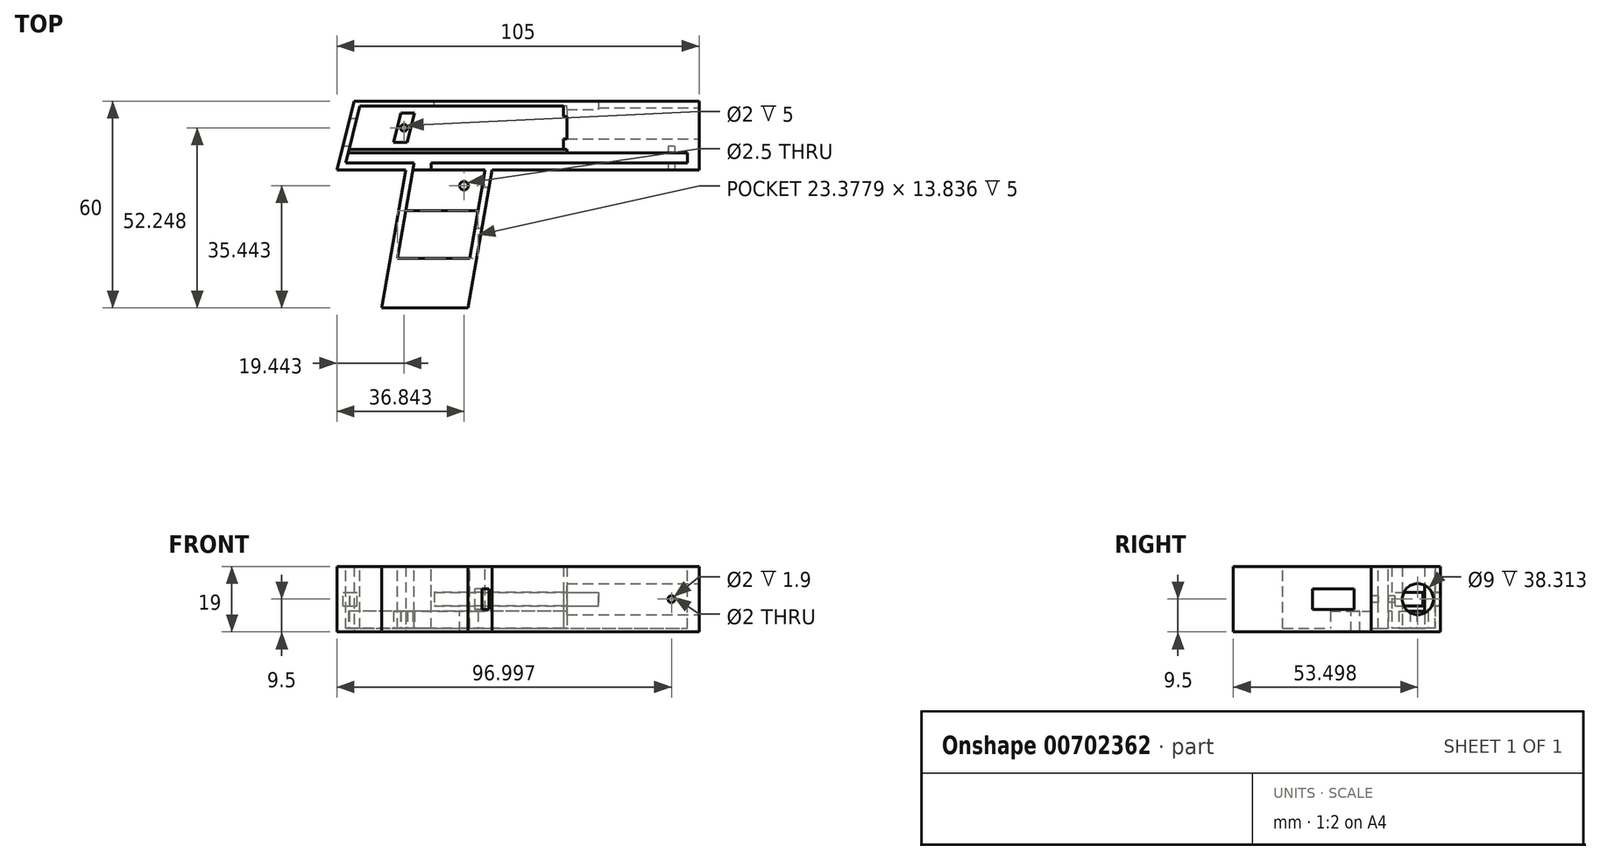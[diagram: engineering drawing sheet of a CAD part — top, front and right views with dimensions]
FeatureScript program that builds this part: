
annotation { "Feature Type Name" : "Feature", "Feature Type Description" : "" }
export const myFeature = defineFeature(function(context is Context, id is Id, definition is map)
    precondition{}
    {
        {
            var Q0;
            Q0=qCreatedBy(makeId("Top.planeOp"),FACE);
            var sketch = newSketch(context, id + "F0", { "sketchPlane" : qUnion([Q0])});
            skLineSegment(sketch, "E0", {"start": v(-39.8, 26.27) * mm, "end": v(60.2, 26.27) * mm});
            skLineSegment(sketch, "E1", {"start": v(60.2, 26.27) * mm, "end": v(60.2, 6.27) * mm});
            skLineSegment(sketch, "E2", {"start": v(60.2, 6.27) * mm, "end": v(0.2, 6.27) * mm});
            skLineSegment(sketch, "E3", {"start": v(0.2, 6.27) * mm, "end": v(-6.86, -33.73) * mm});
            skLineSegment(sketch, "E4", {"start": v(-6.86, -33.73) * mm, "end": v(-31.86, -33.73) * mm});
            skLineSegment(sketch, "E5", {"start": v(-31.86, -33.73) * mm, "end": v(-24.8, 6.27) * mm});
            skLineSegment(sketch, "E6", {"start": v(-24.8, 6.27) * mm, "end": v(-44.8, 6.27) * mm});
            skLineSegment(sketch, "E7", {"start": v(-44.8, 6.27) * mm, "end": v(-39.8, 26.27) * mm});
            skSolve(sketch);
        }
        {
            var Q0;
            Q0=makeQuery(id+"F0.imprint","IMPRINT",FACE,{"disambiguationData":[TD([[makeQuery(id+"F0.imprint","IMPRINT",EDGE,{"derivedFrom":sQuery(id+"F0.wireOp",EDGE,"E0")}),-1.0]])]});
            extrude(context, id + "F1", {"entities" : qUnion([Q0]), "endBound" : BoundingType.SYMMETRIC, "depth" : 19 * mm, "offsetDistance" : 25 * mm});
        }
        {
            var Q0;
            Q0=makeQuery(id+"F1.opExtrude","CAP_FACE",FACE,{"disambiguationData":[OSD([sQuery(id+"F0.wireOp",EDGE,"E0"),sQuery(id+"F0.wireOp",EDGE,"E1"),sQuery(id+"F0.wireOp",EDGE,"E2"),sQuery(id+"F0.wireOp",EDGE,"E3"),sQuery(id+"F0.wireOp",EDGE,"E4"),sQuery(id+"F0.wireOp",EDGE,"E5"),sQuery(id+"F0.wireOp",EDGE,"E6"),sQuery(id+"F0.wireOp",EDGE,"E7")])],"isStart":false});
            var sketch = newSketch(context, id + "F2", { "sketchPlane" : qUnion([Q0])});
            skLineSegment(sketch, "E8", {"start": v(-38.12, 24.77) * mm, "end": v(-42.24, 8.27) * mm});
            skLineSegment(sketch, "E9", {"start": v(-42.24, 8.27) * mm, "end": v(-22.42, 8.27) * mm});
            skLineSegment(sketch, "E10", {"start": v(-22.42, 8.27) * mm, "end": v(-27.3, -19.4) * mm});
            skLineSegment(sketch, "E11", {"start": v(-27.3, -19.4) * mm, "end": v(-6.36, -19.4) * mm});
            skLineSegment(sketch, "E12", {"start": v(-6.36, -19.4) * mm, "end": v(-1.83, 6.27) * mm});
            skLineSegment(sketch, "E13", {"start": v(-1.83, 6.27) * mm, "end": v(-17.42, 6.27) * mm});
            skLineSegment(sketch, "E14", {"start": v(-17.42, 6.27) * mm, "end": v(-17.42, 8.27) * mm});
            skLineSegment(sketch, "E15", {"start": v(-17.42, 8.27) * mm, "end": v(56.88, 8.27) * mm});
            skLineSegment(sketch, "E16", {"start": v(56.88, 8.27) * mm, "end": v(56.88, 11.27) * mm});
            skLineSegment(sketch, "E17", {"start": v(-38.12, 24.77) * mm, "end": v(21.88, 24.77) * mm});
            skLineSegment(sketch, "E18", {"start": v(21.88, 24.77) * mm, "end": v(21.88, 11.27) * mm});
            skLineSegment(sketch, "E19", {"start": v(21.88, 11.27) * mm, "end": v(56.88, 11.27) * mm});
            skSolve(sketch);
        }
        {
            var Q0;
            Q0=makeQuery(id+"F2.imprint","IMPRINT",FACE,{"disambiguationData":[TD([[makeQuery(id+"F2.imprint","IMPRINT",EDGE,{"derivedFrom":sQuery(id+"F2.wireOp",EDGE,"E8")}),1.0]])]});
            extrude(context, id + "F3", {"entities" : qUnion([Q0]), "operationType" : NewBodyOperationType.REMOVE, "oppositeDirection" : true, "depth" : 18 * mm, "offsetDistance" : 25 * mm});
        }
        {
            var Q0;
            Q0=makeQuery(id+"F1.opExtrude","SWEPT_FACE",FACE,{"disambiguationData":[OSD([sQuery(id+"F0.wireOp",EDGE,"E1")])]});
            var sketch = newSketch(context, id + "F4", { "sketchPlane" : qUnion([Q0])});
            skLineSegment(sketch, "E20", {"start": v(26.27, 9.5) * mm, "end": v(6.27, -9.5) * mm, "construction": true});
            skLineSegment(sketch, "E21", {"start": v(26.27, -9.5) * mm, "end": v(6.27, 9.5) * mm, "construction": true});
            skLineSegment(sketch, "E22", {"start": v(16.27, 0) * mm, "end": v(19.77, 0) * mm, "construction": true});
            skCircle(sketch, "E23", {"center": v(19.77, 0) * mm, "radius": 4.5 * mm});
            skSolve(sketch);
        }
        {
            var Q0;
            Q0=makeQuery(id+"F4.imprint","IMPRINT",FACE,{"disambiguationData":[TD([[makeQuery(id+"F4.imprint","IMPRINT",EDGE,{"derivedFrom":sQuery(id+"F4.wireOp",EDGE,"E23")}),1.0]])]});
            extrude(context, id + "F5", {"entities" : qUnion([Q0]), "operationType" : NewBodyOperationType.REMOVE, "oppositeDirection" : true, "depth" : 40 * mm, "offsetDistance" : 25 * mm});
        }
        {
            var Q0;
            Q0=qCreatedBy(makeId("Top.planeOp"),FACE);
            var sketch = newSketch(context, id + "F6", { "sketchPlane" : qUnion([Q0])});
            skLineSegment(sketch, "E24", {"start": v(31.05, 31.36) * mm, "end": v(31.05, 22.47) * mm});
            skLineSegment(sketch, "E25", {"start": v(31.05, 22.47) * mm, "end": v(-16.56, 22.47) * mm});
            skLineSegment(sketch, "E26", {"start": v(-16.56, 22.47) * mm, "end": v(-16.56, 30.77) * mm});
            skLineSegment(sketch, "E27", {"start": v(-16.56, 30.77) * mm, "end": v(31.05, 31.36) * mm});
            skLineSegment(sketch, "E28.bottom", {"start": v(-46.5, 21.27) * mm, "end": v(-35.78, 21.27) * mm});
            skLineSegment(sketch, "E28.top", {"start": v(-46.5, 13.27) * mm, "end": v(-35.78, 13.27) * mm});
            skLineSegment(sketch, "E28.left", {"start": v(-46.5, 21.27) * mm, "end": v(-46.5, 13.27) * mm});
            skLineSegment(sketch, "E28.right", {"start": v(-35.78, 21.27) * mm, "end": v(-35.78, 13.27) * mm});
            skSolve(sketch);
        }
        {
            var Q0;
            Q0=makeQuery(id+"F6.imprint","IMPRINT",FACE,{"disambiguationData":[TD([[makeQuery(id+"F6.imprint","IMPRINT",EDGE,{"derivedFrom":sQuery(id+"F6.wireOp",EDGE,"E24")}),-1.0]])]});
            var Q1;
            Q1=makeQuery(id+"F6.imprint","IMPRINT",FACE,{"disambiguationData":[TD([[makeQuery(id+"F6.imprint","IMPRINT",EDGE,{"derivedFrom":sQuery(id+"F6.wireOp",EDGE,"E28.bottom")}),-1.0]])]});
            extrude(context, id + "F7", {"entities" : qUnion([Q0, Q1]), "operationType" : NewBodyOperationType.REMOVE, "endBound" : BoundingType.SYMMETRIC, "oppositeDirection" : true, "depth" : 4 * mm, "offsetDistance" : 25 * mm});
        }
        {
            var Q0;
            Q0=makeQuery(id+"F3.boolean.opBoolean","COPY",FACE,{"derivedFrom":makeQuery(id+"F3.opExtrude","CAP_FACE",FACE,{"disambiguationData":[OSD([sQuery(id+"F2.wireOp",EDGE,"E8"),sQuery(id+"F2.wireOp",EDGE,"E9"),sQuery(id+"F2.wireOp",EDGE,"E10"),sQuery(id+"F2.wireOp",EDGE,"E11"),sQuery(id+"F2.wireOp",EDGE,"E12"),sQuery(id+"F2.wireOp",EDGE,"E13"),sQuery(id+"F2.wireOp",EDGE,"E14"),sQuery(id+"F2.wireOp",EDGE,"E15"),sQuery(id+"F2.wireOp",EDGE,"E16"),sQuery(id+"F2.wireOp",EDGE,"E17"),sQuery(id+"F2.wireOp",EDGE,"E18"),sQuery(id+"F2.wireOp",EDGE,"E19")])],"isStart":false})});
            var sketch = newSketch(context, id + "F8", { "sketchPlane" : qUnion([Q0])});
            skLineSegment(sketch, "E29", {"start": v(21.88, 11.27) * mm, "end": v(-41.5, 11.27) * mm});
            skLineSegment(sketch, "E30", {"start": v(21.88, 11.27) * mm, "end": v(21.88, 12.27) * mm});
            skLineSegment(sketch, "E31", {"start": v(21.88, 12.27) * mm, "end": v(-41.24, 12.27) * mm});
            skLineSegment(sketch, "E32", {"start": v(-41.24, 12.27) * mm, "end": v(-41.5, 11.27) * mm});
            skLineSegment(sketch, "E33", {"start": v(21.88, 24.77) * mm, "end": v(21.88, 21.77) * mm});
            skLineSegment(sketch, "E34", {"start": v(21.88, 24.77) * mm, "end": v(20.88, 24.77) * mm});
            skLineSegment(sketch, "E35", {"start": v(20.88, 24.77) * mm, "end": v(20.88, 21.77) * mm});
            skLineSegment(sketch, "E36", {"start": v(20.88, 21.77) * mm, "end": v(21.88, 21.77) * mm});
            skLineSegment(sketch, "E37", {"start": v(21.88, 12.27) * mm, "end": v(21.88, 15.27) * mm});
            skLineSegment(sketch, "E38", {"start": v(21.88, 15.27) * mm, "end": v(20.88, 15.27) * mm});
            skLineSegment(sketch, "E39", {"start": v(20.88, 15.27) * mm, "end": v(20.88, 12.27) * mm});
            skLineSegment(sketch, "E40", {"start": v(20.88, 12.27) * mm, "end": v(21.88, 12.27) * mm});
            skLineSegment(sketch, "E41", {"start": v(-1.83, 6.27) * mm, "end": v(-22.77, 6.27) * mm});
            skLineSegment(sketch, "E42", {"start": v(-22.77, 6.27) * mm, "end": v(-24.86, -5.57) * mm});
            skLineSegment(sketch, "E43", {"start": v(-24.86, -5.57) * mm, "end": v(-3.92, -5.57) * mm});
            skLineSegment(sketch, "E44", {"start": v(-3.92, -5.57) * mm, "end": v(-1.83, 6.27) * mm});
            skLineSegment(sketch, "E45", {"start": v(-24.42, 14.27) * mm, "end": v(-22.3, 22.77) * mm});
            skLineSegment(sketch, "E46", {"start": v(-22.3, 22.77) * mm, "end": v(-26.3, 22.77) * mm});
            skLineSegment(sketch, "E47", {"start": v(-26.3, 22.77) * mm, "end": v(-28.42, 14.27) * mm});
            skLineSegment(sketch, "E48", {"start": v(-28.42, 14.27) * mm, "end": v(-24.42, 14.27) * mm});
            skLineSegment(sketch, "E49", {"start": v(-26.3, 22.77) * mm, "end": v(-24.42, 14.27) * mm, "construction": true});
            skLineSegment(sketch, "E50", {"start": v(-28.42, 14.27) * mm, "end": v(-22.3, 22.77) * mm, "construction": true});
            skCircle(sketch, "E51", {"center": v(-25.36, 18.52) * mm, "radius": 1 * mm});
            skSolve(sketch);
        }
        {
            var Q0;
            Q0=makeQuery(id+"F8.imprint","IMPRINT",FACE,{"disambiguationData":[TD([[makeQuery(id+"F8.imprint","IMPRINT",EDGE,{"derivedFrom":sQuery(id+"F8.wireOp",EDGE,"E29")}),-1.0]])]});
            var Q1;
            {var subQ0=sQuery(id+"F8.wireOp",EDGE,"E42");Q1=makeQuery(id+"F8.imprint","IMPRINT",FACE,{"disambiguationData":[TD([[makeQuery(id+"F8.imprint","IMPRINT",EDGE,{"derivedFrom":subQ0}),1.0]])]});}
            var Q2;
            Q2=makeQuery(id+"F8.imprint","IMPRINT",FACE,{"disambiguationData":[TD([[makeQuery(id+"F8.imprint","IMPRINT",EDGE,{"derivedFrom":sQuery(id+"F8.wireOp",EDGE,"E45")}),1.0]])]});
            extrude(context, id + "F9", {"entities" : qUnion([Q0, Q1, Q2]), "operationType" : NewBodyOperationType.ADD, "depth" : 5 * mm, "offsetDistance" : 25 * mm});
        }
        {
            var Q0;
            Q0=makeQuery(id+"F8.imprint","IMPRINT",FACE,{"disambiguationData":[TD([[makeQuery(id+"F8.imprint","IMPRINT",EDGE,{"derivedFrom":sQuery(id+"F8.wireOp",EDGE,"E33")}),-1.0]])]});
            var Q1;
            Q1=makeQuery(id+"F1.opExtrude","CAP_FACE",FACE,{"disambiguationData":[OSD([sQuery(id+"F0.wireOp",EDGE,"E0"),sQuery(id+"F0.wireOp",EDGE,"E1"),sQuery(id+"F0.wireOp",EDGE,"E2"),sQuery(id+"F0.wireOp",EDGE,"E3"),sQuery(id+"F0.wireOp",EDGE,"E4"),sQuery(id+"F0.wireOp",EDGE,"E5"),sQuery(id+"F0.wireOp",EDGE,"E6"),sQuery(id+"F0.wireOp",EDGE,"E7")])],"isStart":false});
            extrude(context, id + "F10", {"entities" : qUnion([Q0]), "operationType" : NewBodyOperationType.ADD, "endBound" : BoundingType.UP_TO_SURFACE, "depth" : 18 * mm, "endBoundEntityFace" : qUnion([Q1]), "offsetDistance" : 25 * mm});
        }
        {
            var Q0;
            Q0=makeQuery(id+"F8.imprint","IMPRINT",FACE,{"disambiguationData":[TD([[makeQuery(id+"F8.imprint","IMPRINT",EDGE,{"derivedFrom":sQuery(id+"F8.wireOp",EDGE,"E37")}),-1.0]])]});
            var Q1;
            {var subQ0=sQuery(id+"F0.wireOp",EDGE,"E7");var subQ1=sQuery(id+"F0.wireOp",EDGE,"E6");var subQ2=sQuery(id+"F0.wireOp",EDGE,"E5");var subQ3=sQuery(id+"F0.wireOp",EDGE,"E4");var subQ4=sQuery(id+"F0.wireOp",EDGE,"E3");var subQ5=sQuery(id+"F0.wireOp",EDGE,"E2");var subQ6=sQuery(id+"F0.wireOp",EDGE,"E1");var subQ7=sQuery(id+"F0.wireOp",EDGE,"E0");Q1=makeQuery(id+"F10.boolean.opBoolean","MERGE",FACE,{"derivedFrom":[makeQuery(id+"F1.opExtrude","CAP_FACE",FACE,{"disambiguationData":[OSD([subQ7,subQ6,subQ5,subQ4,subQ3,subQ2,subQ1,subQ0])],"isStart":false}),makeQuery(id+"F10.opExtrude","CAP_FACE",FACE,{"disambiguationData":[OSD([subQ7,subQ6,subQ5,subQ4,subQ3,subQ2,subQ1,subQ0])],"isStart":false})]});}
            extrude(context, id + "F11", {"entities" : qUnion([Q0]), "operationType" : NewBodyOperationType.ADD, "endBound" : BoundingType.UP_TO_SURFACE, "depth" : 25 * mm, "endBoundEntityFace" : qUnion([Q1]), "offsetDistance" : 25 * mm});
        }
        {
            var Q0;
            Q0=makeQuery(id+"F1.opExtrude","SWEPT_FACE",FACE,{"disambiguationData":[OSD([sQuery(id+"F0.wireOp",EDGE,"E2")])]});
            var sketch = newSketch(context, id + "F12", { "sketchPlane" : qUnion([Q0])});
            skLineSegment(sketch, "E52", {"start": v(60.2, 0) * mm, "end": v(52.2, 0) * mm, "construction": true});
            skCircle(sketch, "E53", {"center": v(52.2, 0) * mm, "radius": 1 * mm});
            skSolve(sketch);
        }
        {
            var Q0;
            Q0=makeQuery(id+"F12.imprint","IMPRINT",FACE,{"disambiguationData":[TD([[makeQuery(id+"F12.imprint","IMPRINT",EDGE,{"derivedFrom":sQuery(id+"F12.wireOp",EDGE,"E53")}),1.0]])]});
            extrude(context, id + "F13", {"entities" : qUnion([Q0]), "operationType" : NewBodyOperationType.REMOVE, "oppositeDirection" : true, "depth" : 6.9 * mm, "offsetDistance" : 25 * mm});
        }
        {
            var Q0;
            Q0=qCreatedBy(makeId("Top.planeOp"),FACE);
            var sketch = newSketch(context, id + "F14", { "sketchPlane" : qUnion([Q0])});
            skLineSegment(sketch, "E54", {"start": v(-9.72, 1.27) * mm, "end": v(7.04, 1.27) * mm});
            skLineSegment(sketch, "E55", {"start": v(7.04, 1.27) * mm, "end": v(7.04, -10.73) * mm});
            skLineSegment(sketch, "E56", {"start": v(7.04, -10.73) * mm, "end": v(-8.95, -10.73) * mm});
            skLineSegment(sketch, "E57", {"start": v(-8.95, -10.73) * mm, "end": v(-9.72, 1.27) * mm});
            skSolve(sketch);
        }
        {
            var Q0;
            Q0=makeQuery(id+"F14.imprint","IMPRINT",FACE,{"disambiguationData":[TD([[makeQuery(id+"F14.imprint","IMPRINT",EDGE,{"derivedFrom":sQuery(id+"F14.wireOp",EDGE,"E54")}),-1.0]])]});
            extrude(context, id + "F15", {"entities" : qUnion([Q0]), "operationType" : NewBodyOperationType.REMOVE, "endBound" : BoundingType.SYMMETRIC, "oppositeDirection" : true, "depth" : 6 * mm, "offsetDistance" : 25 * mm});
        }
        {
            var Q0;
            {var subQ0=sQuery(id+"F2.wireOp",EDGE,"E19");var subQ1=sQuery(id+"F2.wireOp",EDGE,"E16");var subQ2=sQuery(id+"F2.wireOp",EDGE,"E15");var subQ3=sQuery(id+"F2.wireOp",EDGE,"E14");var subQ4=sQuery(id+"F2.wireOp",EDGE,"E13");var subQ5=sQuery(id+"F2.wireOp",EDGE,"E12");var subQ6=sQuery(id+"F2.wireOp",EDGE,"E8");var subQ7=sQuery(id+"F2.wireOp",EDGE,"E9");var subQ8=sQuery(id+"F2.wireOp",EDGE,"E10");var subQ9=sQuery(id+"F2.wireOp",EDGE,"E11");Q0=makeQuery(id+"F9.boolean.opBoolean","SPLIT",FACE,{"disambiguationData":[TD([makeQuery(id+"F3.boolean.opBoolean","COPY",FACE,{"derivedFrom":makeQuery(id+"F3.opExtrude","SWEPT_FACE",FACE,{"disambiguationData":[OSD([subQ7])]})})])],"derivedFrom":makeQuery(id+"F3.boolean.opBoolean","COPY",FACE,{"derivedFrom":makeQuery(id+"F3.opExtrude","CAP_FACE",FACE,{"disambiguationData":[OSD([subQ6,subQ7,subQ8,subQ9,subQ5,subQ4,subQ3,subQ2,subQ1,sQuery(id+"F2.wireOp",EDGE,"E17"),sQuery(id+"F2.wireOp",EDGE,"E18"),subQ0])],"isStart":false})})});}
            var sketch = newSketch(context, id + "F16", { "sketchPlane" : qUnion([Q0])});
            skCircle(sketch, "E58", {"center": v(-7.96, 1.71) * mm, "radius": 1.25 * mm});
            skSolve(sketch);
        }
        {
            var Q0;
            Q0=makeQuery(id+"F16.imprint","IMPRINT",FACE,{"disambiguationData":[TD([[makeQuery(id+"F16.imprint","IMPRINT",EDGE,{"derivedFrom":sQuery(id+"F16.wireOp",EDGE,"E58")}),1.0]])]});
            extrude(context, id + "F17", {"entities" : qUnion([Q0]), "operationType" : NewBodyOperationType.REMOVE, "oppositeDirection" : true, "depth" : 5 * mm, "offsetDistance" : 25 * mm});
        }
        {
            var Q0;
            Q0=makeQuery(id+"F17.boolean.opBoolean","COPY",FACE,{"derivedFrom":makeQuery(id+"F17.opExtrude","CAP_FACE",FACE,{"disambiguationData":[OSD([sQuery(id+"F16.wireOp",EDGE,"E58")])],"isStart":true})});
            extrude(context, id + "F18", {"entities" : qUnion([Q0]), "operationType" : NewBodyOperationType.REMOVE, "oppositeDirection" : true, "depth" : 25 * mm, "offsetDistance" : 25 * mm});
        }
    });
